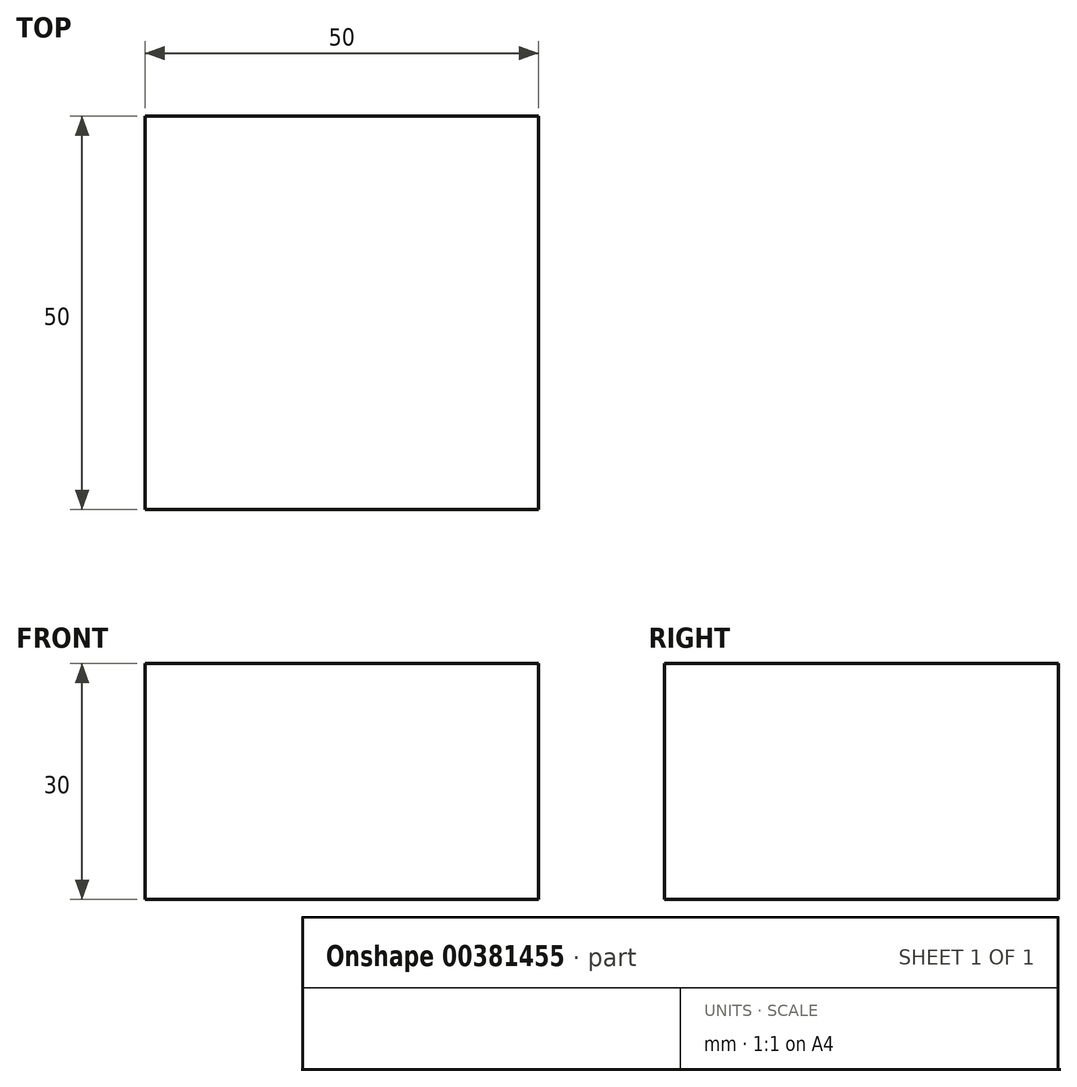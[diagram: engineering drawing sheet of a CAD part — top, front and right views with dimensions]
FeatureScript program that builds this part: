
annotation { "Feature Type Name" : "Feature", "Feature Type Description" : "" }
export const myFeature = defineFeature(function(context is Context, id is Id, definition is map)
    precondition{}
    {
        {
            var Q0;
            Q0=qCreatedBy(makeId("Top.planeOp"),FACE);
            var sketch = newSketch(context, id + "F0", { "sketchPlane" : qUnion([Q0])});
            skLineSegment(sketch, "E0.bottom", {"start": v(25, -25) * mm, "end": v(-25, -25) * mm});
            skLineSegment(sketch, "E0.top", {"start": v(25, 25) * mm, "end": v(-25, 25) * mm});
            skLineSegment(sketch, "E0.left", {"start": v(25, -25) * mm, "end": v(25, 25) * mm});
            skLineSegment(sketch, "E0.right", {"start": v(-25, -25) * mm, "end": v(-25, 25) * mm});
            skPoint(sketch, "E0.middle", {"position": v(0, 0) * mm});
            skSolve(sketch);
        }
        {
            var Q0;
            Q0=makeQuery(id+"F0.imprint","IMPRINT",FACE,{"disambiguationData":[TD([[makeQuery(id+"F0.imprint","IMPRINT",EDGE,{"derivedFrom":sQuery(id+"F0.wireOp",EDGE,"E0.bottom")}),-1.0]])]});
            extrude(context, id + "F1", {"entities" : qUnion([Q0]), "depth" : 30 * mm});
        }
    });
